# Revit family: HARMANN - PIRAX
name_source: partatom
category: Mechanical Equipment
units: mm (PartAtom-declared; Revit-internal decimal feet)

## family parameters
Always vertical = No
Cut with Voids When Loaded = No
Maintain Annotation Orientation = No
OmniClass Number = 23.75.00.00
OmniClass Title = Climate Control (HVAC)
Part Type = Normal
Room Calculation Point = No
Round Connector Dimension = Use Diameter
Shared = No
Work Plane-Based = No

## types (6) — shared parameters
A = 452 mm  [stored 1.48294 ft]
Autor = https://www.archispace.com
B = 340 mm  [stored 1.11549 ft]
Description = Strumieniowy wentylator oddymiający przeznaczony do odprowadzania gorącego powietrza, dymu oraz szkodliwych gazów powstałych podczas pożaru.
G = 47.4 mm  [stored 0.155512 ft]
I = 30 mm  [stored 0.0984252 ft]
I bieg Imax = 1 A
Klasa odporności ogniowej Tmax = 400 oC/2h
L = 1824 mm
Lookup Table Name = PIRAX_G
Manufacturer = Harmann Polska Sp. z o.o.
Temperatura pracy T = 60 °C
Zasilanie Częstotliwość Nominalna = 50 Hz
Zasilanie Ilość faz = 3
Zasilanie Rodzaj Sterowania = II biegi Y/YY
Zasilanie napięcie nominalne Unom = 400 V
zero-valued in all types: Default Elevation

## per-type parameters (varying)
- PIRAX.G CPA 315 D42 F4: C=547 mm  [stored 1.79462 ft]; Ciśnienie akustyczne nominalne II Lpa dB(A)=62 '; E=445 mm  [stored 1.45997 ft]; F=339 mm  [stored 1.1122 ft]; I bieg Lpa dB(A)=47 '; I bieg nmax=1460; J=447 mm  [stored 1.46654 ft]; Kierunek główny. I bieg F=7.00 N; Kierunek główny. I bieg Qmax=2450 m³/h; Kierunek główny. Powietrze Przepływ II=4910 m³/h; Kierunek główny. Siła ciągu II=29.00 N; Kierunek przepływu=Jednokierunkowy; Kierunek rewersyjny. BiegFrev=0.00 N; Kierunek rewersyjny. I bieg Qrev=0 m³/h; Kierunek rewersyjny. Powietrze Przepływ II=0 m³/h; Kierunek rewersyjny. Siła ciągu II=0.00 N; Masa=31.50 kg; N1=2 mm; Numer artykułu=15916601; Obroty maksymalne II (min-1)=2900; Zasilanie Moc maksymalna II=1059 W; Zasilanie natężenie maksymalne II=2 A; Zasilanie. I bieg Pmax=202 W; a=56.5 mm  [stored 0.185367 ft]; b=60 mm  [stored 0.19685 ft]; c=150 mm; d=126.5 mm; e=128 mm  [stored 0.419948 ft]; f=192 mm  [stored 0.629921 ft]; g=234.79 mm; r=158 mm; r2=148 mm  [stored 0.485564 ft]
- PIRAX.G CPA 400 D42 F4: C=635 mm; Ciśnienie akustyczne nominalne II Lpa dB(A)=70 '; E=560 mm  [stored 1.83727 ft]; F=424 mm  [stored 1.39108 ft]; I bieg Lpa dB(A)=51 '; I bieg nmax=1.26; J=535 mm  [stored 1.75525 ft]; Kierunek główny. I bieg F=22.00 N; Kierunek główny. I bieg Qmax=5500 m³/h; Kierunek główny. Powietrze Przepływ II=10830 m³/h; Kierunek główny. Siła ciągu II=87.00 N; Kierunek przepływu=Jednokierunkowy; Kierunek rewersyjny. BiegFrev=0.00 N; Kierunek rewersyjny. I bieg Qrev=0 m³/h; Kierunek rewersyjny. Powietrze Przepływ II=0 m³/h; Kierunek rewersyjny. Siła ciągu II=0.00 N; Masa=46.00 kg; N1=6 mm; Numer artykułu=15908601; Obroty maksymalne II (min-1)=2600; Zasilanie Moc maksymalna II=2875 W; Zasilanie natężenie maksymalne II=5 A; Zasilanie. I bieg Pmax=423 W; a=69.5 mm; b=56.5 mm  [stored 0.185367 ft]; c=189 mm  [stored 0.620079 ft]; d=169 mm; e=167 mm  [stored 0.5479 ft]; f=240 mm  [stored 0.787402 ft]; g=280 mm  [stored 0.918635 ft]; r=201 mm  [stored 0.659449 ft]; r2=191 mm  [stored 0.62664 ft]
- PIRAX CPA 315 D42 F4: C=547 mm  [stored 1.79462 ft]; Ciśnienie akustyczne nominalne II Lpa dB(A)=62 '; E=445 mm  [stored 1.45997 ft]; F=339 mm  [stored 1.1122 ft]; I bieg Lpa dB(A)=47 '; I bieg nmax=1460; J=447 mm  [stored 1.46654 ft]; Kierunek główny. I bieg F=7.00 N; Kierunek główny. I bieg Qmax=2450 m³/h; Kierunek główny. Powietrze Przepływ II=4910 m³/h; Kierunek główny. Siła ciągu II=29.00 N; Kierunek przepływu=Dwukierunkowy; Kierunek rewersyjny. BiegFrev=7.00 N; Kierunek rewersyjny. I bieg Qrev=2400 m³/h; Kierunek rewersyjny. Powietrze Przepływ II=4875 m³/h; Kierunek rewersyjny. Siła ciągu II=28.00 N; Masa=31.50 kg; N1=1 mm; Numer artykułu=15916600; Obroty maksymalne II (min-1)=2900; Zasilanie Moc maksymalna II=1059 W; Zasilanie natężenie maksymalne II=2 A; Zasilanie. I bieg Pmax=202 W; a=56.5 mm  [stored 0.185367 ft]; b=60 mm  [stored 0.19685 ft]; c=150 mm; d=126.5 mm; e=128 mm  [stored 0.419948 ft]; f=192 mm  [stored 0.629921 ft]; g=234.79 mm; r=158 mm; r2=148 mm  [stored 0.485564 ft]
- PIRAX CPA 355 D42 F4: C=587 mm  [stored 1.92585 ft]; Ciśnienie akustyczne nominalne II Lpa dB(A)=67 '; E=505 mm  [stored 1.65682 ft]; F=379 mm  [stored 1.24344 ft]; I bieg Lpa dB(A)=50 '; I bieg nmax=1460; J=489 mm  [stored 1.60433 ft]; Kierunek główny. I bieg F=12.00 N; Kierunek główny. I bieg Qmax=3640 m³/h; Kierunek główny. Powietrze Przepływ II=7330 m³/h; Kierunek główny. Siła ciągu II=50.00 N; Kierunek przepływu=Dwukierunkowy; Kierunek rewersyjny. BiegFrev=12.00 N; Kierunek rewersyjny. I bieg Qrev=3525 m³/h; Kierunek rewersyjny. Powietrze Przepływ II=7050 m³/h; Kierunek rewersyjny. Siła ciągu II=47.00 N; Masa=40.00 kg; N1=3 mm; Numer artykułu=15912300; Obroty maksymalne II (min-1)=2905; Zasilanie Moc maksymalna II=1994 W; Zasilanie natężenie maksymalne II=4 A; Zasilanie. I bieg Pmax=325 W; a=61 mm; b=65 mm  [stored 0.213255 ft]; c=168 mm  [stored 0.551181 ft]; d=142.5 mm  [stored 0.46752 ft]; e=150 mm; f=225 mm  [stored 0.738189 ft]; g=254 mm; r=178 mm  [stored 0.58399 ft]; r2=168 mm  [stored 0.551181 ft]
- PIRAX.G CPA 355 D42 F4: C=587 mm  [stored 1.92585 ft]; Ciśnienie akustyczne nominalne II Lpa dB(A)=670 '; E=505 mm  [stored 1.65682 ft]; F=379 mm  [stored 1.24344 ft]; I bieg Lpa dB(A)=50 '; I bieg nmax=1460; J=489 mm  [stored 1.60433 ft]; Kierunek główny. I bieg F=12.00 N; Kierunek główny. I bieg Qmax=3640 m³/h; Kierunek główny. Powietrze Przepływ II=7330 m³/h; Kierunek główny. Siła ciągu II=50.00 N; Kierunek przepływu=Jednokierunkowy; Kierunek rewersyjny. BiegFrev=0.00 N; Kierunek rewersyjny. I bieg Qrev=0 m³/h; Kierunek rewersyjny. Powietrze Przepływ II=0 m³/h; Kierunek rewersyjny. Siła ciągu II=0.00 N; Masa=40.00 kg; N1=4 mm; Numer artykułu=15912301; Obroty maksymalne II (min-1)=2905; Zasilanie Moc maksymalna II=1994 W; Zasilanie natężenie maksymalne II=4 A; Zasilanie. I bieg Pmax=325 W; a=61 mm; b=65 mm  [stored 0.213255 ft]; c=168 mm  [stored 0.551181 ft]; d=142.5 mm  [stored 0.46752 ft]; e=150 mm; f=225 mm  [stored 0.738189 ft]; g=254 mm; r=178 mm  [stored 0.58399 ft]; r2=168 mm  [stored 0.551181 ft]
- PIRAX CPA 400 D42 F4: C=635 mm; Ciśnienie akustyczne nominalne II Lpa dB(A)=70 '; E=560 mm  [stored 1.83727 ft]; F=424 mm  [stored 1.39108 ft]; I bieg Lpa dB(A)=51 '; I bieg nmax=1460; J=535 mm  [stored 1.75525 ft]; Kierunek główny. I bieg F=22.00 N; Kierunek główny. I bieg Qmax=5500 m³/h; Kierunek główny. Powietrze Przepływ II=10830 m³/h; Kierunek główny. Siła ciągu II=87.00 N; Kierunek przepływu=Dwukierunkowy; Kierunek rewersyjny. BiegFrev=19.00 N; Kierunek rewersyjny. I bieg Qrev=5060 m³/h; Kierunek rewersyjny. Powietrze Przepływ II=10020 m³/h; Kierunek rewersyjny. Siła ciągu II=74.00 N; Masa=46.00 kg; N1=5 mm; Numer artykułu=15908600; Obroty maksymalne II (min-1)=2890; Zasilanie Moc maksymalna II=2875 W; Zasilanie natężenie maksymalne II=5 A; Zasilanie. I bieg Pmax=423 W; a=69.5 mm; b=56.5 mm  [stored 0.185367 ft]; c=189 mm  [stored 0.620079 ft]; d=169 mm; e=167 mm  [stored 0.5479 ft]; f=240 mm  [stored 0.787402 ft]; g=280 mm  [stored 0.918635 ft]; r=201 mm  [stored 0.659449 ft]; r2=191 mm  [stored 0.62664 ft]

note: column(s) folded — value = type name in every type: Model

note: [stored X ft] marks values corroborated as IEEE doubles in the binary element streams (Revit-internal decimal feet)

## geometry (parser evidence)
native form markers: Sweep x2
no freeform markers — native parametric forms only
